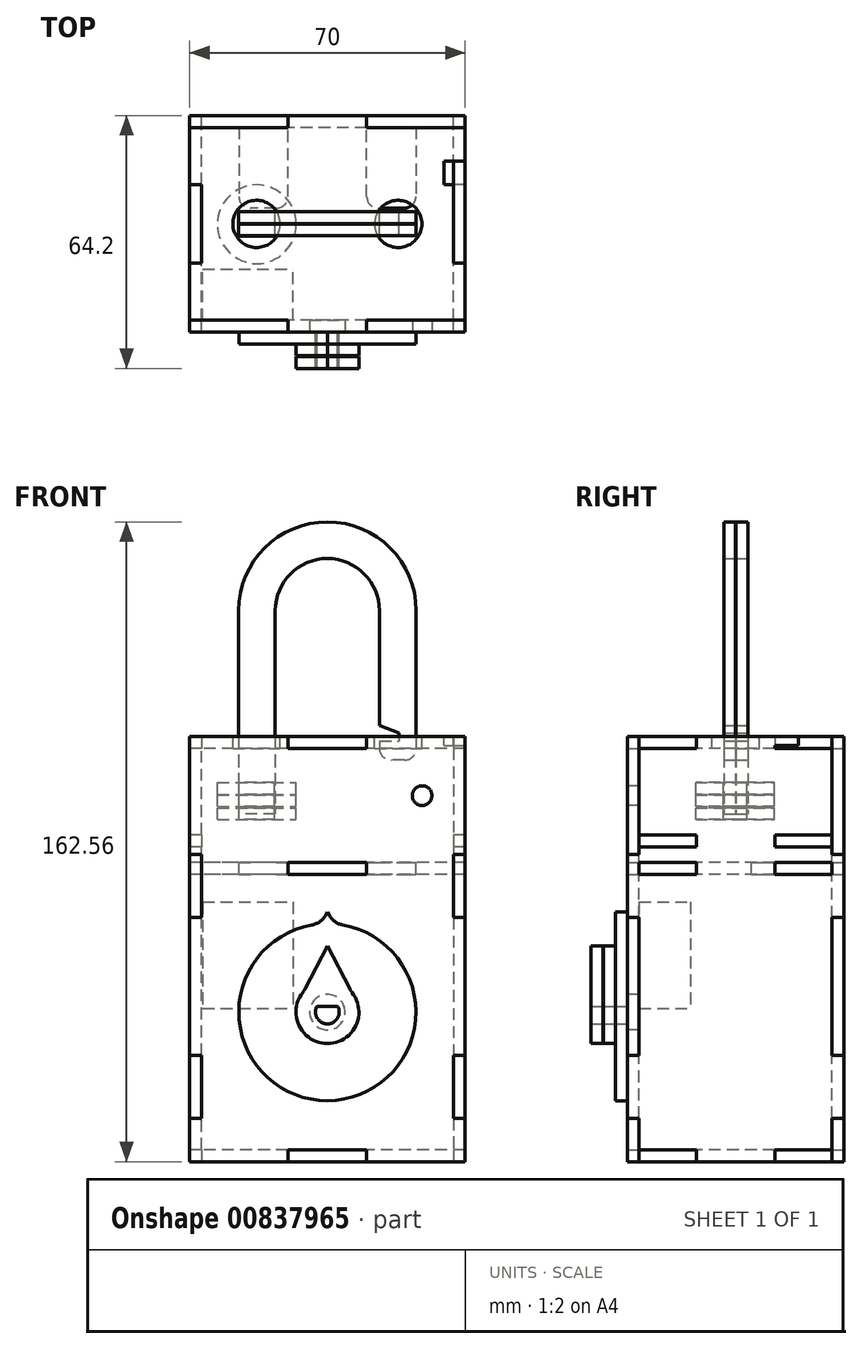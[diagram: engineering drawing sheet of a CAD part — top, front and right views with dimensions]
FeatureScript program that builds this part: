
annotation { "Feature Type Name" : "Feature", "Feature Type Description" : "" }
export const myFeature = defineFeature(function(context is Context, id is Id, definition is map)
    precondition{}
    {
        {
            assignVariable(context, id + "F0", {"name" : "w", "anyValue" : 3});
        }
        {
            var Q0;
            Q0=qCreatedBy(makeId("Front.planeOp"),FACE);
            var sketch = newSketch(context, id + "F1", { "sketchPlane" : qUnion([Q0])});
            skLineSegment(sketch, "E0.bottom", {"start": v(35, -38) * mm, "end": v(10, -38) * mm});
            skLineSegment(sketch, "E0.top", {"start": v(35, 70) * mm, "end": v(10, 70) * mm});
            skLineSegment(sketch, "E0.left", {"start": v(35, -38) * mm, "end": v(35, -27) * mm});
            skPoint(sketch, "E0.middle", {"position": v(0, 0) * mm});
            skLineSegment(sketch, "E1", {"start": v(35, -38) * mm, "end": v(35, -27) * mm, "construction": true});
            skLineSegment(sketch, "E2.bottom", {"start": v(32, -27) * mm, "end": v(35, -27) * mm});
            skLineSegment(sketch, "E2.top", {"start": v(32, -11) * mm, "end": v(35, -11) * mm});
            skLineSegment(sketch, "E2.left", {"start": v(32, -27) * mm, "end": v(32, -11) * mm});
            skLineSegment(sketch, "E3.bottom", {"start": v(35, 24) * mm, "end": v(32, 24) * mm});
            skLineSegment(sketch, "E3.top", {"start": v(35, 40) * mm, "end": v(32, 40) * mm});
            skLineSegment(sketch, "E3.right", {"start": v(32, 24) * mm, "end": v(32, 40) * mm});
            skLineSegment(sketch, "E4.trimOffspring", {"start": v(35, 40) * mm, "end": v(35, 51) * mm});
            skLineSegment(sketch, "E5.trimOffspring", {"start": v(35, -11) * mm, "end": v(35, 24) * mm});
            skLineSegment(sketch, "E6", {"start": v(0, 38) * mm, "end": v(0, -38) * mm, "construction": true});
            skLineSegment(sketch, "E7.bottom", {"start": v(10, 67) * mm, "end": v(-10, 67) * mm});
            skLineSegment(sketch, "E7.left", {"start": v(10, 67) * mm, "end": v(10, 70) * mm});
            skLineSegment(sketch, "E7.right", {"start": v(-10, 67) * mm, "end": v(-10, 70) * mm});
            skLineSegment(sketch, "E8.trimOffspring", {"start": v(-10, 70) * mm, "end": v(-35, 70) * mm});
            skLineSegment(sketch, "E9.bottom", {"start": v(10, -35) * mm, "end": v(-10, -35) * mm});
            skLineSegment(sketch, "E9.left", {"start": v(10, -35) * mm, "end": v(10, -38) * mm});
            skLineSegment(sketch, "E9.right", {"start": v(-10, -35) * mm, "end": v(-10, -38) * mm});
            skLineSegment(sketch, "E10.trimOffspring", {"start": v(-10, -38) * mm, "end": v(-35, -38) * mm});
            skLineSegment(sketch, "E11.MirrorCS", {"start": v(-32, -11) * mm, "end": v(-35, -11) * mm});
            skLineSegment(sketch, "E12.MirrorCS", {"start": v(-32, -27) * mm, "end": v(-35, -27) * mm});
            skLineSegment(sketch, "E13.MirrorCS", {"start": v(-35, 40) * mm, "end": v(-32, 40) * mm});
            skLineSegment(sketch, "E14.MirrorCS", {"start": v(-35, 24) * mm, "end": v(-32, 24) * mm});
            skLineSegment(sketch, "E15.MirrorCS", {"start": v(-35, -38) * mm, "end": v(-35, -27) * mm});
            skLineSegment(sketch, "E16.MirrorCS", {"start": v(-35, -38) * mm, "end": v(-35, -27) * mm, "construction": true});
            skLineSegment(sketch, "E17.MirrorCS", {"start": v(-35, 40) * mm, "end": v(-35, 51) * mm});
            skLineSegment(sketch, "E18.MirrorCS", {"start": v(-35, -11) * mm, "end": v(-35, 24) * mm});
            skLineSegment(sketch, "E19.MirrorCS", {"start": v(-32, 24) * mm, "end": v(-32, 40) * mm});
            skLineSegment(sketch, "E20.MirrorCS", {"start": v(-32, -27) * mm, "end": v(-32, -11) * mm});
            skLineSegment(sketch, "E21", {"start": v(-35, 40) * mm, "end": v(-35, 70) * mm});
            skLineSegment(sketch, "E22", {"start": v(35, 70) * mm, "end": v(35, 40) * mm});
            skSolve(sketch);
        }
        {
            var Q0;
            Q0=makeQuery(id+"F1.imprint","IMPRINT",FACE,{"disambiguationData":[TD([[makeQuery(id+"F1.imprint","IMPRINT",EDGE,{"derivedFrom":sQuery(id+"F1.wireOp",EDGE,"E0.bottom")}),-1.0]])]});
            extrude(context, id + "F2", {"entities" : qUnion([Q0]), "depth" : (getVariable(context, 'w')) * mm, "offsetDistance" : 25 * mm});
        }
        {
            var Q0;
            Q0=makeQuery(id+"F2.opExtrude","SWEPT_FACE",FACE,{"disambiguationData":[OSD([sQuery(id+"F1.wireOp",EDGE,"E0.left")])]});
            var sketch = newSketch(context, id + "F3", { "sketchPlane" : qUnion([Q0])});
            skLineSegment(sketch, "E23.bottom", {"start": v(0, -38) * mm, "end": v(-55, -38) * mm});
            skLineSegment(sketch, "E23.top", {"start": v(0, 70) * mm, "end": v(-55, 70) * mm});
            skLineSegment(sketch, "E23.left", {"start": v(0, -38) * mm, "end": v(0, 70) * mm});
            skLineSegment(sketch, "E23.right", {"start": v(-55, -38) * mm, "end": v(-55, 70) * mm});
            skSolve(sketch);
        }
        {
            var Q0;
            Q0=makeQuery(id+"F2.opExtrude","SWEPT_FACE",FACE,{"disambiguationData":[OSD([sQuery(id+"F1.wireOp",EDGE,"E0.bottom")])]});
            var sketch = newSketch(context, id + "F4", { "sketchPlane" : qUnion([Q0])});
            skLineSegment(sketch, "E24.left", {"start": v(35, 0) * mm, "end": v(35, 17.5) * mm});
            skLineSegment(sketch, "E25.MirrorCS", {"start": v(35, 55) * mm, "end": v(-35, 55) * mm});
            skLineSegment(sketch, "E26.MirrorCS", {"start": v(-35, 0) * mm, "end": v(-35, 17.5) * mm});
            skLineSegment(sketch, "E27.MirrorCS", {"start": v(35, 0) * mm, "end": v(-35, 0) * mm});
            skLineSegment(sketch, "E28", {"start": v(35, 55) * mm, "end": v(32, 55) * mm, "construction": true});
            skLineSegment(sketch, "E29", {"start": v(32, 55) * mm, "end": v(32, 0) * mm, "construction": true});
            skLineSegment(sketch, "E30", {"start": v(-35, 55) * mm, "end": v(-32, 55) * mm, "construction": true});
            skLineSegment(sketch, "E31", {"start": v(-32, 55) * mm, "end": v(-32, 0) * mm, "construction": true});
            skLineSegment(sketch, "E32", {"start": v(-35, 27.5) * mm, "end": v(35, 27.5) * mm, "construction": true});
            skLineSegment(sketch, "E33.bottom", {"start": v(35, 17.5) * mm, "end": v(32, 17.5) * mm});
            skLineSegment(sketch, "E33.top", {"start": v(35, 37.5) * mm, "end": v(32, 37.5) * mm});
            skLineSegment(sketch, "E33.right", {"start": v(32, 17.5) * mm, "end": v(32, 37.5) * mm});
            skLineSegment(sketch, "E34.bottom", {"start": v(-32, 17.5) * mm, "end": v(-35, 17.5) * mm});
            skLineSegment(sketch, "E34.top", {"start": v(-32, 37.5) * mm, "end": v(-35, 37.5) * mm});
            skLineSegment(sketch, "E34.left", {"start": v(-32, 17.5) * mm, "end": v(-32, 37.5) * mm});
            skLineSegment(sketch, "E35.trimOffspring", {"start": v(-35, 37.5) * mm, "end": v(-35, 55) * mm});
            skLineSegment(sketch, "E36.trimOffspring", {"start": v(35, 37.5) * mm, "end": v(35, 55) * mm});
            skSolve(sketch);
        }
        {
            var Q0;
            Q0 = qSketchRegion(id + "F3", true);
            extrude(context, id + "F5", {"entities" : qUnion([Q0]), "oppositeDirection" : true, "depth" : (getVariable(context, 'w')) * mm, "offsetDistance" : 25 * mm});
        }
        {
            var Q0;
            Q0 = qSketchRegion(id + "F4", true);
            extrude(context, id + "F6", {"entities" : qUnion([Q0]), "oppositeDirection" : true, "depth" : (getVariable(context, 'w')) * mm, "offsetDistance" : 25 * mm});
        }
        {
            var Q0;
            Q0=makeQuery(id+"F2.opExtrude","SWEPT_BODY",BODY,{"disambiguationData":[OSD([sQuery(id+"F1.wireOp",EDGE,"E0.bottom"),sQuery(id+"F1.wireOp",EDGE,"E0.top"),sQuery(id+"F1.wireOp",EDGE,"E0.left"),sQuery(id+"F1.wireOp",EDGE,"E2.bottom"),sQuery(id+"F1.wireOp",EDGE,"E2.top"),sQuery(id+"F1.wireOp",EDGE,"E2.left"),sQuery(id+"F1.wireOp",EDGE,"E3.bottom"),sQuery(id+"F1.wireOp",EDGE,"E3.top"),sQuery(id+"F1.wireOp",EDGE,"E3.right"),sQuery(id+"F1.wireOp",EDGE,"E4.trimOffspring"),sQuery(id+"F1.wireOp",EDGE,"E5.trimOffspring"),sQuery(id+"F1.wireOp",EDGE,"E7.bottom"),sQuery(id+"F1.wireOp",EDGE,"E7.left"),sQuery(id+"F1.wireOp",EDGE,"E7.right"),sQuery(id+"F1.wireOp",EDGE,"E8.trimOffspring"),sQuery(id+"F1.wireOp",EDGE,"E9.bottom"),sQuery(id+"F1.wireOp",EDGE,"E9.left"),sQuery(id+"F1.wireOp",EDGE,"E9.right"),sQuery(id+"F1.wireOp",EDGE,"E10.trimOffspring"),sQuery(id+"F1.wireOp",EDGE,"E11.MirrorCS"),sQuery(id+"F1.wireOp",EDGE,"E12.MirrorCS"),sQuery(id+"F1.wireOp",EDGE,"E13.MirrorCS"),sQuery(id+"F1.wireOp",EDGE,"E14.MirrorCS"),sQuery(id+"F1.wireOp",EDGE,"E15.MirrorCS"),sQuery(id+"F1.wireOp",EDGE,"E17.MirrorCS"),sQuery(id+"F1.wireOp",EDGE,"E18.MirrorCS"),sQuery(id+"F1.wireOp",EDGE,"E19.MirrorCS"),sQuery(id+"F1.wireOp",EDGE,"E20.MirrorCS")])]});
            transform(context, id + "F7", {"entities" : qUnion([Q0]), "transformType" : TransformType.TRANSLATION_3D, "dx" : 0 * mm, "dy" : -52 * mm, "dz" : 0 * mm, "makeCopy" : true});
        }
        {
            var Q0;
            Q0=makeQuery(id+"F2.opExtrude","SWEPT_BODY",BODY,{"disambiguationData":[OSD([sQuery(id+"F1.wireOp",EDGE,"E0.bottom"),sQuery(id+"F1.wireOp",EDGE,"E0.top"),sQuery(id+"F1.wireOp",EDGE,"E0.left"),sQuery(id+"F1.wireOp",EDGE,"E2.bottom"),sQuery(id+"F1.wireOp",EDGE,"E2.top"),sQuery(id+"F1.wireOp",EDGE,"E2.left"),sQuery(id+"F1.wireOp",EDGE,"E3.bottom"),sQuery(id+"F1.wireOp",EDGE,"E3.top"),sQuery(id+"F1.wireOp",EDGE,"E3.right"),sQuery(id+"F1.wireOp",EDGE,"E4.trimOffspring"),sQuery(id+"F1.wireOp",EDGE,"E5.trimOffspring"),sQuery(id+"F1.wireOp",EDGE,"E7.bottom"),sQuery(id+"F1.wireOp",EDGE,"E7.left"),sQuery(id+"F1.wireOp",EDGE,"E7.right"),sQuery(id+"F1.wireOp",EDGE,"E8.trimOffspring"),sQuery(id+"F1.wireOp",EDGE,"E9.bottom"),sQuery(id+"F1.wireOp",EDGE,"E9.left"),sQuery(id+"F1.wireOp",EDGE,"E9.right"),sQuery(id+"F1.wireOp",EDGE,"E10.trimOffspring"),sQuery(id+"F1.wireOp",EDGE,"E11.MirrorCS"),sQuery(id+"F1.wireOp",EDGE,"E12.MirrorCS"),sQuery(id+"F1.wireOp",EDGE,"E13.MirrorCS"),sQuery(id+"F1.wireOp",EDGE,"E14.MirrorCS"),sQuery(id+"F1.wireOp",EDGE,"E15.MirrorCS"),sQuery(id+"F1.wireOp",EDGE,"E17.MirrorCS"),sQuery(id+"F1.wireOp",EDGE,"E18.MirrorCS"),sQuery(id+"F1.wireOp",EDGE,"E19.MirrorCS"),sQuery(id+"F1.wireOp",EDGE,"E20.MirrorCS")])]});
            var Q1;
            Q1=makeQuery(id+"F7.opPattern","COPY",BODY,{"derivedFrom":makeQuery(id+"F2.opExtrude","SWEPT_BODY",BODY,{"disambiguationData":[OSD([sQuery(id+"F1.wireOp",EDGE,"E0.bottom"),sQuery(id+"F1.wireOp",EDGE,"E0.top"),sQuery(id+"F1.wireOp",EDGE,"E0.left"),sQuery(id+"F1.wireOp",EDGE,"E2.bottom"),sQuery(id+"F1.wireOp",EDGE,"E2.top"),sQuery(id+"F1.wireOp",EDGE,"E2.left"),sQuery(id+"F1.wireOp",EDGE,"E3.bottom"),sQuery(id+"F1.wireOp",EDGE,"E3.top"),sQuery(id+"F1.wireOp",EDGE,"E3.right"),sQuery(id+"F1.wireOp",EDGE,"E4.trimOffspring"),sQuery(id+"F1.wireOp",EDGE,"E5.trimOffspring"),sQuery(id+"F1.wireOp",EDGE,"E7.bottom"),sQuery(id+"F1.wireOp",EDGE,"E7.left"),sQuery(id+"F1.wireOp",EDGE,"E7.right"),sQuery(id+"F1.wireOp",EDGE,"E8.trimOffspring"),sQuery(id+"F1.wireOp",EDGE,"E9.bottom"),sQuery(id+"F1.wireOp",EDGE,"E9.left"),sQuery(id+"F1.wireOp",EDGE,"E9.right"),sQuery(id+"F1.wireOp",EDGE,"E10.trimOffspring"),sQuery(id+"F1.wireOp",EDGE,"E11.MirrorCS"),sQuery(id+"F1.wireOp",EDGE,"E12.MirrorCS"),sQuery(id+"F1.wireOp",EDGE,"E13.MirrorCS"),sQuery(id+"F1.wireOp",EDGE,"E14.MirrorCS"),sQuery(id+"F1.wireOp",EDGE,"E15.MirrorCS"),sQuery(id+"F1.wireOp",EDGE,"E17.MirrorCS"),sQuery(id+"F1.wireOp",EDGE,"E18.MirrorCS"),sQuery(id+"F1.wireOp",EDGE,"E19.MirrorCS"),sQuery(id+"F1.wireOp",EDGE,"E20.MirrorCS")])]}),"instanceName":"1"});
            var Q2;
            Q2=makeQuery(id+"F5.opExtrude","SWEPT_BODY",BODY,{"disambiguationData":[OSD([sQuery(id+"F3.wireOp",EDGE,"E23.bottom"),sQuery(id+"F3.wireOp",EDGE,"E23.top"),sQuery(id+"F3.wireOp",EDGE,"E23.left"),sQuery(id+"F3.wireOp",EDGE,"E23.right")])]});
            var Q3;
            Q3=makeQuery(id+"F6.opExtrude","SWEPT_BODY",BODY,{"disambiguationData":[OSD([sQuery(id+"F4.wireOp",EDGE,"E24.left"),sQuery(id+"F4.wireOp",EDGE,"E25.MirrorCS"),sQuery(id+"F4.wireOp",EDGE,"E26.MirrorCS"),sQuery(id+"F4.wireOp",EDGE,"E27.MirrorCS")])]});
            booleanBodies(context, id + "F8", {"operationType" : BooleanOperationType.SUBTRACTION, "tools" : qUnion([Q0, Q1]), "targets" : qUnion([Q2, Q3]), "keepTools" : true});
        }
        {
            var Q0;
            Q0=makeQuery(id+"F5.opExtrude","SWEPT_BODY",BODY,{"disambiguationData":[OSD([sQuery(id+"F3.wireOp",EDGE,"E23.bottom"),sQuery(id+"F3.wireOp",EDGE,"E23.top"),sQuery(id+"F3.wireOp",EDGE,"E23.left"),sQuery(id+"F3.wireOp",EDGE,"E23.right")])]});
            transform(context, id + "F9", {"entities" : qUnion([Q0]), "transformType" : TransformType.TRANSLATION_3D, "dx" : -67 * mm, "dy" : 0 * mm, "dz" : 0 * mm, "makeCopy" : true});
        }
        {
            var Q0;
            Q0=makeQuery(id+"F6.opExtrude","SWEPT_BODY",BODY,{"disambiguationData":[OSD([sQuery(id+"F4.wireOp",EDGE,"E24.left"),sQuery(id+"F4.wireOp",EDGE,"E25.MirrorCS"),sQuery(id+"F4.wireOp",EDGE,"E26.MirrorCS"),sQuery(id+"F4.wireOp",EDGE,"E27.MirrorCS"),sQuery(id+"F4.wireOp",EDGE,"E33.bottom"),sQuery(id+"F4.wireOp",EDGE,"E33.top"),sQuery(id+"F4.wireOp",EDGE,"E33.right"),sQuery(id+"F4.wireOp",EDGE,"E34.bottom"),sQuery(id+"F4.wireOp",EDGE,"E34.top"),sQuery(id+"F4.wireOp",EDGE,"E34.left"),sQuery(id+"F4.wireOp",EDGE,"E35.trimOffspring"),sQuery(id+"F4.wireOp",EDGE,"E36.trimOffspring")])]});
            var Q1;
            Q1=makeQuery(id+"F9.opPattern","COPY",BODY,{"derivedFrom":makeQuery(id+"F5.opExtrude","SWEPT_BODY",BODY,{"disambiguationData":[OSD([sQuery(id+"F3.wireOp",EDGE,"E23.bottom"),sQuery(id+"F3.wireOp",EDGE,"E23.top"),sQuery(id+"F3.wireOp",EDGE,"E23.left"),sQuery(id+"F3.wireOp",EDGE,"E23.right")])]}),"instanceName":"1"});
            var Q2;
            Q2=makeQuery(id+"F5.opExtrude","SWEPT_BODY",BODY,{"disambiguationData":[OSD([sQuery(id+"F3.wireOp",EDGE,"E23.bottom"),sQuery(id+"F3.wireOp",EDGE,"E23.top"),sQuery(id+"F3.wireOp",EDGE,"E23.left"),sQuery(id+"F3.wireOp",EDGE,"E23.right")])]});
            booleanBodies(context, id + "F10", {"operationType" : BooleanOperationType.SUBTRACTION, "tools" : qUnion([Q0]), "targets" : qUnion([Q1, Q2]), "keepTools" : true});
        }
        {
            var Q0;
            Q0=makeQuery(id+"F6.opExtrude","SWEPT_BODY",BODY,{"disambiguationData":[OSD([sQuery(id+"F4.wireOp",EDGE,"E24.left"),sQuery(id+"F4.wireOp",EDGE,"E25.MirrorCS"),sQuery(id+"F4.wireOp",EDGE,"E26.MirrorCS"),sQuery(id+"F4.wireOp",EDGE,"E27.MirrorCS"),sQuery(id+"F4.wireOp",EDGE,"E33.bottom"),sQuery(id+"F4.wireOp",EDGE,"E33.top"),sQuery(id+"F4.wireOp",EDGE,"E33.right"),sQuery(id+"F4.wireOp",EDGE,"E34.bottom"),sQuery(id+"F4.wireOp",EDGE,"E34.top"),sQuery(id+"F4.wireOp",EDGE,"E34.left"),sQuery(id+"F4.wireOp",EDGE,"E35.trimOffspring"),sQuery(id+"F4.wireOp",EDGE,"E36.trimOffspring")])]});
            transform(context, id + "F11", {"entities" : qUnion([Q0]), "transformType" : TransformType.TRANSLATION_3D, "dx" : 0 * mm, "dy" : 0 * mm, "dz" : 80 * mm, "makeCopy" : true});
        }
        {
            var Q0;
            Q0=makeQuery(id+"F11.opPattern","COPY",BODY,{"derivedFrom":makeQuery(id+"F6.opExtrude","SWEPT_BODY",BODY,{"disambiguationData":[OSD([sQuery(id+"F4.wireOp",EDGE,"E24.left"),sQuery(id+"F4.wireOp",EDGE,"E25.MirrorCS"),sQuery(id+"F4.wireOp",EDGE,"E26.MirrorCS"),sQuery(id+"F4.wireOp",EDGE,"E27.MirrorCS"),sQuery(id+"F4.wireOp",EDGE,"E33.bottom"),sQuery(id+"F4.wireOp",EDGE,"E33.top"),sQuery(id+"F4.wireOp",EDGE,"E33.right"),sQuery(id+"F4.wireOp",EDGE,"E34.bottom"),sQuery(id+"F4.wireOp",EDGE,"E34.top"),sQuery(id+"F4.wireOp",EDGE,"E34.left"),sQuery(id+"F4.wireOp",EDGE,"E35.trimOffspring"),sQuery(id+"F4.wireOp",EDGE,"E36.trimOffspring")])]}),"instanceName":"1"});
            var Q1;
            Q1=makeQuery(id+"F9.opPattern","COPY",BODY,{"derivedFrom":makeQuery(id+"F5.opExtrude","SWEPT_BODY",BODY,{"disambiguationData":[OSD([sQuery(id+"F3.wireOp",EDGE,"E23.bottom"),sQuery(id+"F3.wireOp",EDGE,"E23.top"),sQuery(id+"F3.wireOp",EDGE,"E23.left"),sQuery(id+"F3.wireOp",EDGE,"E23.right")])]}),"instanceName":"1"});
            var Q2;
            Q2=makeQuery(id+"F5.opExtrude","SWEPT_BODY",BODY,{"disambiguationData":[OSD([sQuery(id+"F3.wireOp",EDGE,"E23.bottom"),sQuery(id+"F3.wireOp",EDGE,"E23.top"),sQuery(id+"F3.wireOp",EDGE,"E23.left"),sQuery(id+"F3.wireOp",EDGE,"E23.right")])]});
            booleanBodies(context, id + "F12", {"operationType" : BooleanOperationType.SUBTRACTION, "tools" : qUnion([Q0]), "targets" : qUnion([Q1, Q2]), "keepTools" : true});
        }
        {
            var Q0;
            Q0=makeQuery(id+"F11.opPattern","COPY",FACE,{"derivedFrom":makeQuery(id+"F6.opExtrude","CAP_FACE",FACE,{"disambiguationData":[OSD([sQuery(id+"F4.wireOp",EDGE,"E24.left"),sQuery(id+"F4.wireOp",EDGE,"E25.MirrorCS"),sQuery(id+"F4.wireOp",EDGE,"E26.MirrorCS"),sQuery(id+"F4.wireOp",EDGE,"E27.MirrorCS"),sQuery(id+"F4.wireOp",EDGE,"E33.bottom"),sQuery(id+"F4.wireOp",EDGE,"E33.top"),sQuery(id+"F4.wireOp",EDGE,"E33.right"),sQuery(id+"F4.wireOp",EDGE,"E34.bottom"),sQuery(id+"F4.wireOp",EDGE,"E34.top"),sQuery(id+"F4.wireOp",EDGE,"E34.left"),sQuery(id+"F4.wireOp",EDGE,"E35.trimOffspring"),sQuery(id+"F4.wireOp",EDGE,"E36.trimOffspring")])],"isStart":false}),"instanceName":"1"});
            var sketch = newSketch(context, id + "F13", { "sketchPlane" : qUnion([Q0])});
            skLineSegment(sketch, "E37", {"start": v(0, -27.5) * mm, "end": v(18, -27.5) * mm, "construction": true});
            skLineSegment(sketch, "E38", {"start": v(18, -27.5) * mm, "end": v(-18, -27.5) * mm, "construction": true});
            skCircle(sketch, "E39", {"center": v(-18, -27.5) * mm, "radius": 6 * mm});
            skCircle(sketch, "E40", {"center": v(18, -27.5) * mm, "radius": 6 * mm});
            skSolve(sketch);
        }
        {
            var Q0;
            Q0=makeQuery(id+"F13.imprint","IMPRINT",FACE,{"disambiguationData":[TD([[makeQuery(id+"F13.imprint","IMPRINT",EDGE,{"derivedFrom":sQuery(id+"F13.wireOp",EDGE,"E39")}),1.0]])]});
            var Q1;
            Q1=makeQuery(id+"F13.imprint","IMPRINT",FACE,{"disambiguationData":[TD([[makeQuery(id+"F13.imprint","IMPRINT",EDGE,{"derivedFrom":sQuery(id+"F13.wireOp",EDGE,"E40")}),1.0]])]});
            var Q2;
            Q2=sQuery(id+"F13.wireOp",EDGE,"E39");
            var Q3;
            Q3=sQuery(id+"F13.wireOp",EDGE,"E40");
            extrude(context, id + "F14", {"entities" : qUnion([Q0, Q1]), "operationType" : NewBodyOperationType.REMOVE, "surfaceEntities" : qUnion([Q2, Q3]), "oppositeDirection" : true, "depth" : 25 * mm, "offsetDistance" : 25 * mm});
        }
        {
            var Q0;
            Q0=makeQuery(id+"F7.opPattern","COPY",FACE,{"derivedFrom":makeQuery(id+"F2.opExtrude","CAP_FACE",FACE,{"disambiguationData":[OSD([sQuery(id+"F1.wireOp",EDGE,"E0.bottom"),sQuery(id+"F1.wireOp",EDGE,"E0.top"),sQuery(id+"F1.wireOp",EDGE,"E0.left"),sQuery(id+"F1.wireOp",EDGE,"E2.bottom"),sQuery(id+"F1.wireOp",EDGE,"E2.top"),sQuery(id+"F1.wireOp",EDGE,"E2.left"),sQuery(id+"F1.wireOp",EDGE,"E3.bottom"),sQuery(id+"F1.wireOp",EDGE,"E3.top"),sQuery(id+"F1.wireOp",EDGE,"E3.right"),sQuery(id+"F1.wireOp",EDGE,"E4.trimOffspring"),sQuery(id+"F1.wireOp",EDGE,"E5.trimOffspring"),sQuery(id+"F1.wireOp",EDGE,"E7.bottom"),sQuery(id+"F1.wireOp",EDGE,"E7.left"),sQuery(id+"F1.wireOp",EDGE,"E7.right"),sQuery(id+"F1.wireOp",EDGE,"E8.trimOffspring"),sQuery(id+"F1.wireOp",EDGE,"E9.bottom"),sQuery(id+"F1.wireOp",EDGE,"E9.left"),sQuery(id+"F1.wireOp",EDGE,"E9.right"),sQuery(id+"F1.wireOp",EDGE,"E10.trimOffspring"),sQuery(id+"F1.wireOp",EDGE,"E11.MirrorCS"),sQuery(id+"F1.wireOp",EDGE,"E12.MirrorCS"),sQuery(id+"F1.wireOp",EDGE,"E13.MirrorCS"),sQuery(id+"F1.wireOp",EDGE,"E14.MirrorCS"),sQuery(id+"F1.wireOp",EDGE,"E15.MirrorCS"),sQuery(id+"F1.wireOp",EDGE,"E17.MirrorCS"),sQuery(id+"F1.wireOp",EDGE,"E18.MirrorCS"),sQuery(id+"F1.wireOp",EDGE,"E19.MirrorCS"),sQuery(id+"F1.wireOp",EDGE,"E20.MirrorCS")])],"isStart":false}),"instanceName":"1"});
            var sketch = newSketch(context, id + "F15", { "sketchPlane" : qUnion([Q0])});
            skArc(sketch, "E41", {"start": v(-6.24, 5) * mm, "mid": v(0, -8) * mm, "end": v(6.24, 5) * mm});
            skArc(sketch, "E42", {"start": v(-3.93, 22.15) * mm, "mid": v(0.02, -22.5) * mm, "end": v(3.9, 22.16) * mm});
            skLineSegment(sketch, "E43", {"start": v(0, 0) * mm, "end": v(0, 25.4) * mm, "construction": true});
            skLineSegment(sketch, "E44", {"start": v(0, 25.4) * mm, "end": v(-0.46, 24.6) * mm});
            skLineSegment(sketch, "E45", {"start": v(0, 25.4) * mm, "end": v(0.5, 24.53) * mm});
            skPoint(sketch, "E46.visualSharp", {"position": v(-1.7, 22.44) * mm});
            skArc(sketch, "E46.filletArc", {"start": v(-3.93, 22.15) * mm, "mid": v(-1.92, 23) * mm, "end": v(-0.46, 24.6) * mm});
            skPoint(sketch, "E47.visualSharp", {"position": v(1.72, 22.43) * mm});
            skArc(sketch, "E47.filletArc", {"start": v(0.5, 24.53) * mm, "mid": v(1.94, 22.97) * mm, "end": v(3.9, 22.16) * mm});
            skCircle(sketch, "E48", {"center": v(0, 0) * mm, "radius": 4.5 * mm});
            skArc(sketch, "E49", {"start": v(-2.6, 1.5) * mm, "mid": v(0, -3) * mm, "end": v(2.6, 1.5) * mm});
            skLineSegment(sketch, "E50", {"start": v(0, 0) * mm, "end": v(0, 1.5) * mm, "construction": true});
            skLineSegment(sketch, "E51", {"start": v(0, 1.5) * mm, "end": v(2.6, 1.5) * mm, "construction": true});
            skLineSegment(sketch, "E52", {"start": v(2.6, 1.5) * mm, "end": v(-2.6, 1.5) * mm});
            skLineSegment(sketch, "E53", {"start": v(0, 16.88) * mm, "end": v(-5.7, 5.83) * mm});
            skLineSegment(sketch, "E54", {"start": v(5.7, 5.83) * mm, "end": v(0, 16.88) * mm});
            skPoint(sketch, "E55.visualSharp", {"position": v(-5.96, 5.34) * mm});
            skArc(sketch, "E55.filletArc", {"start": v(-6.24, 5) * mm, "mid": v(-5.95, 5.4) * mm, "end": v(-5.7, 5.83) * mm});
            skPoint(sketch, "E56.visualSharp", {"position": v(5.96, 5.34) * mm});
            skArc(sketch, "E56.filletArc", {"start": v(5.7, 5.83) * mm, "mid": v(5.95, 5.4) * mm, "end": v(6.24, 5) * mm});
            skSolve(sketch);
        }
        {
            var Q0;
            Q0=makeQuery(id+"F15.imprint","IMPRINT",FACE,{"disambiguationData":[TD([[makeQuery(id+"F15.imprint","IMPRINT",EDGE,{"derivedFrom":sQuery(id+"F15.wireOp",EDGE,"E48")}),1.0]])]});
            var Q1;
            Q1=makeQuery(id+"F15.imprint","IMPRINT",FACE,{"disambiguationData":[TD([[makeQuery(id+"F15.imprint","IMPRINT",EDGE,{"derivedFrom":sQuery(id+"F15.wireOp",EDGE,"E49")}),1.0]])]});
            var Q2;
            Q2=sQuery(id+"F15.wireOp",EDGE,"E41");
            extrude(context, id + "F16", {"entities" : qUnion([Q0, Q1]), "operationType" : NewBodyOperationType.REMOVE, "surfaceEntities" : qUnion([Q2]), "oppositeDirection" : true, "depth" : 5 * mm, "offsetDistance" : 25 * mm});
        }
        {
            var Q0;
            Q0=makeQuery(id+"F15.imprint","IMPRINT",FACE,{"disambiguationData":[TD([[makeQuery(id+"F15.imprint","IMPRINT",EDGE,{"derivedFrom":sQuery(id+"F15.wireOp",EDGE,"E41")}),-1.0]])]});
            var Q1;
            Q1=makeQuery(id+"F15.imprint","IMPRINT",FACE,{"disambiguationData":[TD([[makeQuery(id+"F15.imprint","IMPRINT",EDGE,{"derivedFrom":sQuery(id+"F15.wireOp",EDGE,"E41")}),1.0]])]});
            var Q2;
            Q2=makeQuery(id+"F15.imprint","IMPRINT",FACE,{"disambiguationData":[TD([[makeQuery(id+"F15.imprint","IMPRINT",EDGE,{"derivedFrom":sQuery(id+"F15.wireOp",EDGE,"E48")}),1.0]])]});
            extrude(context, id + "F17", {"entities" : qUnion([Q0, Q1, Q2]), "depth" : (getVariable(context, 'w')) * mm, "offsetDistance" : 25 * mm});
        }
        {
            var Q0;
            Q0=makeQuery(id+"F15.imprint","IMPRINT",FACE,{"disambiguationData":[TD([[makeQuery(id+"F15.imprint","IMPRINT",EDGE,{"derivedFrom":sQuery(id+"F15.wireOp",EDGE,"E41")}),1.0]])]});
            var Q1;
            Q1=makeQuery(id+"F15.imprint","IMPRINT",FACE,{"disambiguationData":[TD([[makeQuery(id+"F15.imprint","IMPRINT",EDGE,{"derivedFrom":sQuery(id+"F15.wireOp",EDGE,"E48")}),1.0]])]});
            var Q2;
            Q2=sQuery(id+"F15.wireOp",EDGE,"E41");
            var Q3;
            Q3=sQuery(id+"F15.wireOp",EDGE,"E48");
            extrude(context, id + "F18", {"entities" : qUnion([Q0, Q1]), "surfaceEntities" : qUnion([Q2, Q3]), "depth" : 6 * mm, "offsetDistance" : 25 * mm, "hasSecondDirection" : true, "secondDirectionOppositeDirection" : false, "secondDirectionDepth" : 3 * mm});
        }
        {
            var Q0;
            Q0=makeQuery(id+"F15.imprint","IMPRINT",FACE,{"disambiguationData":[TD([[makeQuery(id+"F15.imprint","IMPRINT",EDGE,{"derivedFrom":sQuery(id+"F15.wireOp",EDGE,"E42")}),-1.0]])]});
            var sketch = newSketch(context, id + "F19", { "sketchPlane" : qUnion([Q0])});
            skArc(sketch, "E57", {"start": v(13.24, 102) * mm, "mid": v(0, 115.24) * mm, "end": v(-13.24, 102) * mm});
            skLineSegment(sketch, "E58", {"start": v(-13.24, 102) * mm, "end": v(-13.24, 54.66) * mm});
            skLineSegment(sketch, "E59", {"start": v(13.24, 102) * mm, "end": v(13.24, 72.88) * mm});
            skLineSegment(sketch, "E60", {"start": v(22.56, 102) * mm, "end": v(22.56, 67) * mm});
            skLineSegment(sketch, "E61", {"start": v(-22.56, 102) * mm, "end": v(-22.56, 50.39) * mm});
            skArc(sketch, "E62.trimOffspring", {"start": v(22.56, 102) * mm, "mid": v(0, 124.56) * mm, "end": v(-22.56, 102) * mm});
            skLineSegment(sketch, "E63", {"start": v(-13.24, 54.66) * mm, "end": v(-13.24, 50.39) * mm});
            skLineSegment(sketch, "E64", {"start": v(19.56, 64) * mm, "end": v(16.24, 64) * mm});
            skPoint(sketch, "E65.visualSharp", {"position": v(22.56, 64) * mm});
            skArc(sketch, "E65.filletArc", {"start": v(19.56, 64) * mm, "mid": v(21.68, 64.88) * mm, "end": v(22.56, 67) * mm});
            skPoint(sketch, "E66.visualSharp", {"position": v(13.24, 64) * mm});
            skArc(sketch, "E66.filletArc", {"start": v(13.24, 67) * mm, "mid": v(14.12, 64.88) * mm, "end": v(16.24, 64) * mm});
            skLineSegment(sketch, "E67.top", {"start": v(13.24, 68.88) * mm, "end": v(18.24, 68.88) * mm});
            skLineSegment(sketch, "E67.right", {"start": v(18.24, 70.88) * mm, "end": v(18.24, 68.88) * mm});
            skLineSegment(sketch, "E68", {"start": v(18.24, 70.88) * mm, "end": v(13.24, 72.88) * mm});
            skPoint(sketch, "E69.orphan", {"position": v(18.24, 72.88) * mm});
            skLineSegment(sketch, "E70.trimOffspring", {"start": v(13.24, 68.88) * mm, "end": v(13.24, 67) * mm});
            skLineSegment(sketch, "E71", {"start": v(-13.24, 50.39) * mm, "end": v(-22.56, 50.39) * mm});
            skSolve(sketch);
        }
        {
            var Q0;
            {var subQ8=sQuery(id+"F19.wireOp",EDGE,"E57");Q0=makeQuery(id+"F19.imprint","IMPRINT",FACE,{"disambiguationData":[TD([[makeQuery(id+"F19.imprint","IMPRINT",EDGE,{"derivedFrom":subQ8}),-1.0]])]});}
            var Q1;
            Q1=makeQuery(id+"F19.imprint","IMPRINT",FACE,{"disambiguationData":[TD([[makeQuery(id+"F19.imprint","IMPRINT",EDGE,{"derivedFrom":sQuery(id+"F19.wireOp",EDGE,"E64")}),-1.0]])]});
            var Q2;
            {var subQ4=sQuery(id+"F19.wireOp",EDGE,"E63");Q2=makeQuery(id+"F19.imprint","IMPRINT",FACE,{"disambiguationData":[TD([[makeQuery(id+"F19.imprint","IMPRINT",EDGE,{"derivedFrom":subQ4}),-1.0]])]});}
            extrude(context, id + "F20", {"entities" : qUnion([Q0, Q1, Q2]), "depth" : (getVariable(context, 'w')) * mm, "offsetDistance" : 25 * mm});
        }
        {
            var Q0;
            Q0=makeQuery(id+"F20.opExtrude","SWEPT_BODY",BODY,{"disambiguationData":[OSD([sQuery(id+"F19.wireOp",EDGE,"E57"),sQuery(id+"F19.wireOp",EDGE,"E58"),sQuery(id+"F19.wireOp",EDGE,"E59"),sQuery(id+"F19.wireOp",EDGE,"E60"),sQuery(id+"F19.wireOp",EDGE,"E61"),sQuery(id+"F19.wireOp",EDGE,"E62.trimOffspring"),sQuery(id+"F19.wireOp",EDGE,"cZzg15dB-Nbx1-w7XY-uspp-L3SwX9o6WefN"),sQuery(id+"F19.wireOp",EDGE,"treZg7xo-gXZQ-1tuO-3OQy-4RqyVRKiaork"),sQuery(id+"F19.wireOp",EDGE,"E63"),sQuery(id+"F19.wireOp",EDGE,"R1Tcik5A-y3kw-4I4Y-LH2I-3jnCuK7BDUFd"),sQuery(id+"F19.wireOp",EDGE,"49c95767-d3e9-4f83-846b-7651090b67ab.trimOffspring")])]});
            deleteBodies(context, id + "F21", {"entities" : qUnion([Q0])});
        }
        {
            var Q0;
            Q0=makeQuery(id+"F4.imprint","IMPRINT",FACE,{"disambiguationData":[TD([[makeQuery(id+"F4.imprint","IMPRINT",EDGE,{"derivedFrom":sQuery(id+"F4.wireOp",EDGE,"E25.MirrorCS")}),1.0]])]});
            var sketch = newSketch(context, id + "F22", { "sketchPlane" : qUnion([Q0])});
            skCircle(sketch, "E72", {"center": v(-17.94, 27.59) * mm, "radius": 10 * mm});
            skLineSegment(sketch, "E73.bottom", {"start": v(-13.44, 24.59) * mm, "end": v(-22.44, 24.59) * mm});
            skLineSegment(sketch, "E73.top", {"start": v(-13.44, 30.59) * mm, "end": v(-22.44, 30.59) * mm});
            skLineSegment(sketch, "E73.left", {"start": v(-13.44, 24.59) * mm, "end": v(-13.44, 30.59) * mm});
            skLineSegment(sketch, "E73.right", {"start": v(-22.44, 24.59) * mm, "end": v(-22.44, 30.59) * mm});
            skSolve(sketch);
        }
        {
            var Q0;
            Q0=makeQuery(id+"F22.imprint","IMPRINT",FACE,{"disambiguationData":[TD([[makeQuery(id+"F22.imprint","IMPRINT",EDGE,{"derivedFrom":sQuery(id+"F22.wireOp",EDGE,"E72")}),1.0]])]});
            extrude(context, id + "F23", {"entities" : qUnion([Q0]), "depth" : (getVariable(context, 'w')) * mm, "offsetDistance" : 25 * mm});
        }
        {
            var Q0;
            Q0=makeQuery(id+"F23.opExtrude","SWEPT_BODY",BODY,{"disambiguationData":[OSD([sQuery(id+"F22.wireOp",EDGE,"E72"),sQuery(id+"F22.wireOp",EDGE,"E73.bottom"),sQuery(id+"F22.wireOp",EDGE,"E73.top"),sQuery(id+"F22.wireOp",EDGE,"E73.left"),sQuery(id+"F22.wireOp",EDGE,"E73.right")])]});
            transform(context, id + "F24", {"entities" : qUnion([Q0]), "transformType" : TransformType.TRANSLATION_3D, "dx" : 0 * mm, "dy" : 0 * mm, "dz" : 68.2 * mm, "makeCopy" : true});
        }
        {
            var Q0;
            Q0=makeQuery(id+"F24.opPattern","COPY",BODY,{"derivedFrom":makeQuery(id+"F23.opExtrude","SWEPT_BODY",BODY,{"disambiguationData":[OSD([sQuery(id+"F22.wireOp",EDGE,"E72"),sQuery(id+"F22.wireOp",EDGE,"E73.bottom"),sQuery(id+"F22.wireOp",EDGE,"E73.top"),sQuery(id+"F22.wireOp",EDGE,"E73.left"),sQuery(id+"F22.wireOp",EDGE,"E73.right")])]}),"instanceName":"1"});
            transform(context, id + "F25", {"entities" : qUnion([Q0]), "transformType" : TransformType.TRANSLATION_3D, "dx" : 0 * mm, "dy" : 0 * mm, "dz" : -3.3 * mm, "makeCopy" : true});
        }
        {
            var Q0;
            Q0=makeQuery(id+"F25.opPattern","COPY",BODY,{"derivedFrom":makeQuery(id+"F24.opPattern","COPY",BODY,{"derivedFrom":makeQuery(id+"F23.opExtrude","SWEPT_BODY",BODY,{"disambiguationData":[OSD([sQuery(id+"F22.wireOp",EDGE,"E72"),sQuery(id+"F22.wireOp",EDGE,"E73.bottom"),sQuery(id+"F22.wireOp",EDGE,"E73.top"),sQuery(id+"F22.wireOp",EDGE,"E73.left"),sQuery(id+"F22.wireOp",EDGE,"E73.right")])]}),"instanceName":"1"}),"instanceName":"1"});
            transform(context, id + "F26", {"entities" : qUnion([Q0]), "transformType" : TransformType.TRANSLATION_3D, "dx" : 0 * mm, "dy" : 0 * mm, "dz" : 6.4 * mm, "makeCopy" : true});
        }
        {
            var Q0;
            Q0=makeQuery(id+"F23.opExtrude","SWEPT_BODY",BODY,{"disambiguationData":[OSD([sQuery(id+"F22.wireOp",EDGE,"E72"),sQuery(id+"F22.wireOp",EDGE,"E73.bottom"),sQuery(id+"F22.wireOp",EDGE,"E73.top"),sQuery(id+"F22.wireOp",EDGE,"E73.left"),sQuery(id+"F22.wireOp",EDGE,"E73.right")])]});
            deleteBodies(context, id + "F27", {"entities" : qUnion([Q0])});
        }
        {
            var Q0;
            Q0=makeQuery(id+"F5.opExtrude","CAP_FACE",FACE,{"disambiguationData":[OSD([sQuery(id+"F3.wireOp",EDGE,"E23.bottom"),sQuery(id+"F3.wireOp",EDGE,"E23.top"),sQuery(id+"F3.wireOp",EDGE,"E23.left"),sQuery(id+"F3.wireOp",EDGE,"E23.right")])],"isStart":true});
            var sketch = newSketch(context, id + "F28", { "sketchPlane" : qUnion([Q0])});
            skLineSegment(sketch, "E74.bottom", {"start": v(-11.5, 42.7) * mm, "end": v(-22.5, 42.7) * mm});
            skLineSegment(sketch, "E74.top", {"start": v(-11.5, 53.7) * mm, "end": v(-22.5, 53.7) * mm});
            skLineSegment(sketch, "E74.left", {"start": v(-11.5, 42.7) * mm, "end": v(-11.5, 53.7) * mm});
            skLineSegment(sketch, "E74.right", {"start": v(-22.5, 42.7) * mm, "end": v(-22.5, 53.7) * mm});
            skPoint(sketch, "E74.middle", {"position": v(-17, 48.2) * mm});
            skPoint(sketch, "E74.middle.positionSnap0", {"position": v(-27.5, 70) * mm});
            skPoint(sketch, "E74.centerSnap0", {"position": v(-27.5, 70) * mm});
            skSolve(sketch);
        }
        {
            var Q0;
            Q0=makeQuery(id+"F28.imprint","IMPRINT",FACE,{"disambiguationData":[TD([[makeQuery(id+"F28.imprint","IMPRINT",EDGE,{"derivedFrom":sQuery(id+"F28.wireOp",EDGE,"E74.bottom")}),-1.0]])]});
            extrude(context, id + "F29", {"entities" : qUnion([Q0]), "operationType" : NewBodyOperationType.REMOVE, "oppositeDirection" : true, "depth" : 5.4 * mm, "offsetDistance" : 25 * mm});
        }
        {
            var Q0;
            Q0=makeQuery(id+"F18.opExtrude","SWEPT_BODY",BODY,{"disambiguationData":[OSD([sQuery(id+"F15.wireOp",EDGE,"E41"),sQuery(id+"F15.wireOp",EDGE,"E49"),sQuery(id+"F15.wireOp",EDGE,"E52"),sQuery(id+"F15.wireOp",EDGE,"E53"),sQuery(id+"F15.wireOp",EDGE,"E54"),sQuery(id+"F15.wireOp",EDGE,"E55.filletArc"),sQuery(id+"F15.wireOp",EDGE,"E56.filletArc")])]});
            transform(context, id + "F30", {"entities" : qUnion([Q0]), "transformType" : TransformType.TRANSLATION_3D, "dx" : 0 * mm, "dy" : -3.2 * mm, "dz" : 0 * mm, "makeCopy" : true});
        }
        {
            var Q0;
            Q0=makeQuery(id+"F5.opExtrude","CAP_FACE",FACE,{"disambiguationData":[OSD([sQuery(id+"F3.wireOp",EDGE,"E23.bottom"),sQuery(id+"F3.wireOp",EDGE,"E23.top"),sQuery(id+"F3.wireOp",EDGE,"E23.left"),sQuery(id+"F3.wireOp",EDGE,"E23.right")])],"isStart":false});
            var sketch = newSketch(context, id + "F31", { "sketchPlane" : qUnion([Q0])});
            skLineSegment(sketch, "E75.bottom", {"start": v(52, 27.96) * mm, "end": v(39, 27.96) * mm});
            skLineSegment(sketch, "E75.top", {"start": v(52, 0.96) * mm, "end": v(39, 0.96) * mm});
            skLineSegment(sketch, "E75.left", {"start": v(52, 27.96) * mm, "end": v(52, 0.96) * mm});
            skLineSegment(sketch, "E75.right", {"start": v(39, 27.96) * mm, "end": v(39, 0.96) * mm});
            skSolve(sketch);
        }
        {
            var Q0;
            {var subQ9=sQuery(id+"F31.wireOp",EDGE,"E75.bottom");Q0=makeQuery(id+"F31.imprint","IMPRINT",FACE,{"disambiguationData":[TD([[makeQuery(id+"F31.imprint","IMPRINT",EDGE,{"derivedFrom":subQ9}),1.0]])]});}
            extrude(context, id + "F32", {"entities" : qUnion([Q0]), "depth" : 63.7 * mm, "offsetDistance" : 25 * mm, "hasSecondDirection" : true, "secondDirectionOppositeDirection" : false, "secondDirectionDepth" : (63.7 - 23) * mm});
        }
        {
            var Q0;
            Q0=makeQuery(id+"F15.imprint","IMPRINT",FACE,{"disambiguationData":[TD([[makeQuery(id+"F15.imprint","IMPRINT",EDGE,{"derivedFrom":sQuery(id+"F15.wireOp",EDGE,"E42")}),-1.0]])]});
            var sketch = newSketch(context, id + "F33", { "sketchPlane" : qUnion([Q0])});
            skCircle(sketch, "E76", {"center": v(24.06, 55) * mm, "radius": 2.5 * mm});
            skSolve(sketch);
        }
        {
            var Q0;
            Q0=makeQuery(id+"F33.imprint","IMPRINT",FACE,{"disambiguationData":[TD([[makeQuery(id+"F33.imprint","IMPRINT",EDGE,{"derivedFrom":sQuery(id+"F33.wireOp",EDGE,"E76")}),1.0]])]});
            var Q1;
            Q1=sQuery(id+"F33.wireOp",EDGE,"E76");
            extrude(context, id + "F34", {"entities" : qUnion([Q0]), "operationType" : NewBodyOperationType.REMOVE, "surfaceEntities" : qUnion([Q1]), "oppositeDirection" : true, "depth" : 6.1 * mm, "offsetDistance" : 25 * mm});
        }
        {
            var Q0;
            Q0=makeQuery(id+"F11.opPattern","COPY",BODY,{"derivedFrom":makeQuery(id+"F6.opExtrude","SWEPT_BODY",BODY,{"disambiguationData":[OSD([sQuery(id+"F4.wireOp",EDGE,"E24.left"),sQuery(id+"F4.wireOp",EDGE,"E25.MirrorCS"),sQuery(id+"F4.wireOp",EDGE,"E26.MirrorCS"),sQuery(id+"F4.wireOp",EDGE,"E27.MirrorCS"),sQuery(id+"F4.wireOp",EDGE,"E33.bottom"),sQuery(id+"F4.wireOp",EDGE,"E33.top"),sQuery(id+"F4.wireOp",EDGE,"E33.right"),sQuery(id+"F4.wireOp",EDGE,"E34.bottom"),sQuery(id+"F4.wireOp",EDGE,"E34.top"),sQuery(id+"F4.wireOp",EDGE,"E34.left"),sQuery(id+"F4.wireOp",EDGE,"E35.trimOffspring"),sQuery(id+"F4.wireOp",EDGE,"E36.trimOffspring")])]}),"instanceName":"1"});
            var Q1;
            Q1=makeQuery(id+"F11.opPattern","COPY",FACE,{"derivedFrom":makeQuery(id+"F6.opExtrude","CAP_FACE",FACE,{"disambiguationData":[OSD([sQuery(id+"F4.wireOp",EDGE,"E24.left"),sQuery(id+"F4.wireOp",EDGE,"E25.MirrorCS"),sQuery(id+"F4.wireOp",EDGE,"E26.MirrorCS"),sQuery(id+"F4.wireOp",EDGE,"E27.MirrorCS"),sQuery(id+"F4.wireOp",EDGE,"E33.bottom"),sQuery(id+"F4.wireOp",EDGE,"E33.top"),sQuery(id+"F4.wireOp",EDGE,"E33.right"),sQuery(id+"F4.wireOp",EDGE,"E34.bottom"),sQuery(id+"F4.wireOp",EDGE,"E34.top"),sQuery(id+"F4.wireOp",EDGE,"E34.left"),sQuery(id+"F4.wireOp",EDGE,"E35.trimOffspring"),sQuery(id+"F4.wireOp",EDGE,"E36.trimOffspring")])],"isStart":false}),"instanceName":"1"});
            transform(context, id + "F35", {"entities" : qUnion([Q0]), "transformType" : TransformType.TRANSLATION_DISTANCE, "transformDirection" : qUnion([Q1]), "distance" : 25 * mm, "makeCopy" : false});
        }
        {
            var Q0;
            Q0=makeQuery(id+"FCm0gpzPxwSbBdX_7.opPattern","COPY",BODY,{"derivedFrom":makeQuery(id+"F20.opExtrude","SWEPT_BODY",BODY,{"disambiguationData":[OSD([sQuery(id+"F1.wireOp",EDGE,"E0.top"),sQuery(id+"F19.wireOp",EDGE,"E57"),sQuery(id+"F19.wireOp",EDGE,"E58"),sQuery(id+"F19.wireOp",EDGE,"E59"),sQuery(id+"F19.wireOp",EDGE,"E60"),sQuery(id+"F19.wireOp",EDGE,"E61"),sQuery(id+"F19.wireOp",EDGE,"E62.trimOffspring"),sQuery(id+"F19.wireOp",EDGE,"treZg7xo-gXZQ-1tuO-3OQy-4RqyVRKiaork"),sQuery(id+"F19.wireOp",EDGE,"E63"),sQuery(id+"F19.wireOp",EDGE,"49c95767-d3e9-4f83-846b-7651090b67ab.trimOffspring")])]}),"instanceName":"1"});
            var Q1;
            Q1=makeQuery(id+"F26.opPattern","COPY",BODY,{"derivedFrom":makeQuery(id+"F25.opPattern","COPY",BODY,{"derivedFrom":makeQuery(id+"F24.opPattern","COPY",BODY,{"derivedFrom":makeQuery(id+"F23.opExtrude","SWEPT_BODY",BODY,{"disambiguationData":[OSD([sQuery(id+"F22.wireOp",EDGE,"E72"),sQuery(id+"F22.wireOp",EDGE,"E73.bottom"),sQuery(id+"F22.wireOp",EDGE,"E73.top"),sQuery(id+"F22.wireOp",EDGE,"E73.left"),sQuery(id+"F22.wireOp",EDGE,"E73.right")])]}),"instanceName":"1"}),"instanceName":"1"}),"instanceName":"1"});
            var Q2;
            Q2=makeQuery(id+"F24.opPattern","COPY",BODY,{"derivedFrom":makeQuery(id+"F23.opExtrude","SWEPT_BODY",BODY,{"disambiguationData":[OSD([sQuery(id+"F22.wireOp",EDGE,"E72"),sQuery(id+"F22.wireOp",EDGE,"E73.bottom"),sQuery(id+"F22.wireOp",EDGE,"E73.top"),sQuery(id+"F22.wireOp",EDGE,"E73.left"),sQuery(id+"F22.wireOp",EDGE,"E73.right")])]}),"instanceName":"1"});
            var Q3;
            Q3=makeQuery(id+"F25.opPattern","COPY",BODY,{"derivedFrom":makeQuery(id+"F24.opPattern","COPY",BODY,{"derivedFrom":makeQuery(id+"F23.opExtrude","SWEPT_BODY",BODY,{"disambiguationData":[OSD([sQuery(id+"F22.wireOp",EDGE,"E72"),sQuery(id+"F22.wireOp",EDGE,"E73.bottom"),sQuery(id+"F22.wireOp",EDGE,"E73.top"),sQuery(id+"F22.wireOp",EDGE,"E73.left"),sQuery(id+"F22.wireOp",EDGE,"E73.right")])]}),"instanceName":"1"}),"instanceName":"1"});
            var Q4;
            Q4=qCreatedBy(makeId("Top.planeOp"),FACE);
            transform(context, id + "F36", {"entities" : qUnion([Q0, Q1, Q2, Q3]), "transformType" : TransformType.TRANSLATION_DISTANCE, "transformDirection" : qUnion([Q4]), "distance" : 25 * mm, "makeCopy" : false});
        }
        {
            var Q0;
            Q0=makeQuery(id+"F6.opExtrude","SWEPT_BODY",BODY,{"disambiguationData":[OSD([sQuery(id+"F4.wireOp",EDGE,"E24.left"),sQuery(id+"F4.wireOp",EDGE,"E25.MirrorCS"),sQuery(id+"F4.wireOp",EDGE,"E26.MirrorCS"),sQuery(id+"F4.wireOp",EDGE,"E27.MirrorCS"),sQuery(id+"F4.wireOp",EDGE,"E33.bottom"),sQuery(id+"F4.wireOp",EDGE,"E33.top"),sQuery(id+"F4.wireOp",EDGE,"E33.right"),sQuery(id+"F4.wireOp",EDGE,"E34.bottom"),sQuery(id+"F4.wireOp",EDGE,"E34.top"),sQuery(id+"F4.wireOp",EDGE,"E34.left"),sQuery(id+"F4.wireOp",EDGE,"E35.trimOffspring"),sQuery(id+"F4.wireOp",EDGE,"E36.trimOffspring")])]});
            transform(context, id + "F37", {"entities" : qUnion([Q0]), "transformType" : TransformType.TRANSLATION_3D, "dx" : 0 * mm, "dy" : 0 * mm, "dz" : 73 * mm, "makeCopy" : true});
        }
        {
            var Q0;
            Q0=makeQuery(id+"F37.opPattern","COPY",BODY,{"derivedFrom":makeQuery(id+"F6.opExtrude","SWEPT_BODY",BODY,{"disambiguationData":[OSD([sQuery(id+"F4.wireOp",EDGE,"E24.left"),sQuery(id+"F4.wireOp",EDGE,"E25.MirrorCS"),sQuery(id+"F4.wireOp",EDGE,"E26.MirrorCS"),sQuery(id+"F4.wireOp",EDGE,"E27.MirrorCS"),sQuery(id+"F4.wireOp",EDGE,"E33.bottom"),sQuery(id+"F4.wireOp",EDGE,"E33.top"),sQuery(id+"F4.wireOp",EDGE,"E33.right"),sQuery(id+"F4.wireOp",EDGE,"E34.bottom"),sQuery(id+"F4.wireOp",EDGE,"E34.top"),sQuery(id+"F4.wireOp",EDGE,"E34.left"),sQuery(id+"F4.wireOp",EDGE,"E35.trimOffspring"),sQuery(id+"F4.wireOp",EDGE,"E36.trimOffspring")])]}),"instanceName":"1"});
            var Q1;
            Q1=makeQuery(id+"F7.opPattern","COPY",BODY,{"derivedFrom":makeQuery(id+"F2.opExtrude","SWEPT_BODY",BODY,{"disambiguationData":[OSD([sQuery(id+"F1.wireOp",EDGE,"E0.bottom"),sQuery(id+"F1.wireOp",EDGE,"E0.top"),sQuery(id+"F1.wireOp",EDGE,"E0.left"),sQuery(id+"F1.wireOp",EDGE,"E2.bottom"),sQuery(id+"F1.wireOp",EDGE,"E2.top"),sQuery(id+"F1.wireOp",EDGE,"E2.left"),sQuery(id+"F1.wireOp",EDGE,"E3.bottom"),sQuery(id+"F1.wireOp",EDGE,"E3.top"),sQuery(id+"F1.wireOp",EDGE,"E3.right"),sQuery(id+"F1.wireOp",EDGE,"E5.trimOffspring"),sQuery(id+"F1.wireOp",EDGE,"E7.bottom"),sQuery(id+"F1.wireOp",EDGE,"E7.left"),sQuery(id+"F1.wireOp",EDGE,"E7.right"),sQuery(id+"F1.wireOp",EDGE,"E8.trimOffspring"),sQuery(id+"F1.wireOp",EDGE,"E9.bottom"),sQuery(id+"F1.wireOp",EDGE,"E9.left"),sQuery(id+"F1.wireOp",EDGE,"E9.right"),sQuery(id+"F1.wireOp",EDGE,"E10.trimOffspring"),sQuery(id+"F1.wireOp",EDGE,"E11.MirrorCS"),sQuery(id+"F1.wireOp",EDGE,"E12.MirrorCS"),sQuery(id+"F1.wireOp",EDGE,"E13.MirrorCS"),sQuery(id+"F1.wireOp",EDGE,"E14.MirrorCS"),sQuery(id+"F1.wireOp",EDGE,"E15.MirrorCS"),sQuery(id+"F1.wireOp",EDGE,"E18.MirrorCS"),sQuery(id+"F1.wireOp",EDGE,"E19.MirrorCS"),sQuery(id+"F1.wireOp",EDGE,"E20.MirrorCS"),sQuery(id+"F1.wireOp",EDGE,"E21"),sQuery(id+"F1.wireOp",EDGE,"E22")])]}),"instanceName":"1"});
            var Q2;
            Q2=makeQuery(id+"F5.opExtrude","SWEPT_BODY",BODY,{"disambiguationData":[OSD([sQuery(id+"F3.wireOp",EDGE,"E23.bottom"),sQuery(id+"F3.wireOp",EDGE,"E23.top"),sQuery(id+"F3.wireOp",EDGE,"E23.left"),sQuery(id+"F3.wireOp",EDGE,"E23.right")])]});
            var Q3;
            Q3=makeQuery(id+"F9.opPattern","COPY",BODY,{"derivedFrom":makeQuery(id+"F5.opExtrude","SWEPT_BODY",BODY,{"disambiguationData":[OSD([sQuery(id+"F3.wireOp",EDGE,"E23.bottom"),sQuery(id+"F3.wireOp",EDGE,"E23.top"),sQuery(id+"F3.wireOp",EDGE,"E23.left"),sQuery(id+"F3.wireOp",EDGE,"E23.right")])]}),"instanceName":"1"});
            var Q4;
            Q4=makeQuery(id+"F2.opExtrude","SWEPT_BODY",BODY,{"disambiguationData":[OSD([sQuery(id+"F1.wireOp",EDGE,"E0.bottom"),sQuery(id+"F1.wireOp",EDGE,"E0.top"),sQuery(id+"F1.wireOp",EDGE,"E0.left"),sQuery(id+"F1.wireOp",EDGE,"E2.bottom"),sQuery(id+"F1.wireOp",EDGE,"E2.top"),sQuery(id+"F1.wireOp",EDGE,"E2.left"),sQuery(id+"F1.wireOp",EDGE,"E3.bottom"),sQuery(id+"F1.wireOp",EDGE,"E3.top"),sQuery(id+"F1.wireOp",EDGE,"E3.right"),sQuery(id+"F1.wireOp",EDGE,"E5.trimOffspring"),sQuery(id+"F1.wireOp",EDGE,"E7.bottom"),sQuery(id+"F1.wireOp",EDGE,"E7.left"),sQuery(id+"F1.wireOp",EDGE,"E7.right"),sQuery(id+"F1.wireOp",EDGE,"E8.trimOffspring"),sQuery(id+"F1.wireOp",EDGE,"E9.bottom"),sQuery(id+"F1.wireOp",EDGE,"E9.left"),sQuery(id+"F1.wireOp",EDGE,"E9.right"),sQuery(id+"F1.wireOp",EDGE,"E10.trimOffspring"),sQuery(id+"F1.wireOp",EDGE,"E11.MirrorCS"),sQuery(id+"F1.wireOp",EDGE,"E12.MirrorCS"),sQuery(id+"F1.wireOp",EDGE,"E13.MirrorCS"),sQuery(id+"F1.wireOp",EDGE,"E14.MirrorCS"),sQuery(id+"F1.wireOp",EDGE,"E15.MirrorCS"),sQuery(id+"F1.wireOp",EDGE,"E18.MirrorCS"),sQuery(id+"F1.wireOp",EDGE,"E19.MirrorCS"),sQuery(id+"F1.wireOp",EDGE,"E20.MirrorCS"),sQuery(id+"F1.wireOp",EDGE,"E21"),sQuery(id+"F1.wireOp",EDGE,"E22")])]});
            booleanBodies(context, id + "F38", {"operationType" : BooleanOperationType.SUBTRACTION, "tools" : qUnion([Q0]), "targets" : qUnion([Q1, Q2, Q3, Q4]), "keepTools" : true});
        }
        {
            var Q0;
            Q0=makeQuery(id+"F11.opPattern","COPY",BODY,{"derivedFrom":makeQuery(id+"F6.opExtrude","SWEPT_BODY",BODY,{"disambiguationData":[OSD([sQuery(id+"F4.wireOp",EDGE,"E24.left"),sQuery(id+"F4.wireOp",EDGE,"E25.MirrorCS"),sQuery(id+"F4.wireOp",EDGE,"E26.MirrorCS"),sQuery(id+"F4.wireOp",EDGE,"E27.MirrorCS"),sQuery(id+"F4.wireOp",EDGE,"E33.bottom"),sQuery(id+"F4.wireOp",EDGE,"E33.top"),sQuery(id+"F4.wireOp",EDGE,"E33.right"),sQuery(id+"F4.wireOp",EDGE,"E34.bottom"),sQuery(id+"F4.wireOp",EDGE,"E34.top"),sQuery(id+"F4.wireOp",EDGE,"E34.left"),sQuery(id+"F4.wireOp",EDGE,"E35.trimOffspring"),sQuery(id+"F4.wireOp",EDGE,"E36.trimOffspring")])]}),"instanceName":"1"});
            var Q1;
            Q1=makeQuery(id+"F5.opExtrude","SWEPT_BODY",BODY,{"disambiguationData":[OSD([sQuery(id+"F3.wireOp",EDGE,"E23.bottom"),sQuery(id+"F3.wireOp",EDGE,"E23.top"),sQuery(id+"F3.wireOp",EDGE,"E23.left"),sQuery(id+"F3.wireOp",EDGE,"E23.right")])]});
            var Q2;
            Q2=makeQuery(id+"F7.opPattern","COPY",BODY,{"derivedFrom":makeQuery(id+"F2.opExtrude","SWEPT_BODY",BODY,{"disambiguationData":[OSD([sQuery(id+"F1.wireOp",EDGE,"E0.bottom"),sQuery(id+"F1.wireOp",EDGE,"E0.top"),sQuery(id+"F1.wireOp",EDGE,"E0.left"),sQuery(id+"F1.wireOp",EDGE,"E2.bottom"),sQuery(id+"F1.wireOp",EDGE,"E2.top"),sQuery(id+"F1.wireOp",EDGE,"E2.left"),sQuery(id+"F1.wireOp",EDGE,"E3.bottom"),sQuery(id+"F1.wireOp",EDGE,"E3.top"),sQuery(id+"F1.wireOp",EDGE,"E3.right"),sQuery(id+"F1.wireOp",EDGE,"E5.trimOffspring"),sQuery(id+"F1.wireOp",EDGE,"E7.bottom"),sQuery(id+"F1.wireOp",EDGE,"E7.left"),sQuery(id+"F1.wireOp",EDGE,"E7.right"),sQuery(id+"F1.wireOp",EDGE,"E8.trimOffspring"),sQuery(id+"F1.wireOp",EDGE,"E9.bottom"),sQuery(id+"F1.wireOp",EDGE,"E9.left"),sQuery(id+"F1.wireOp",EDGE,"E9.right"),sQuery(id+"F1.wireOp",EDGE,"E10.trimOffspring"),sQuery(id+"F1.wireOp",EDGE,"E11.MirrorCS"),sQuery(id+"F1.wireOp",EDGE,"E12.MirrorCS"),sQuery(id+"F1.wireOp",EDGE,"E13.MirrorCS"),sQuery(id+"F1.wireOp",EDGE,"E14.MirrorCS"),sQuery(id+"F1.wireOp",EDGE,"E15.MirrorCS"),sQuery(id+"F1.wireOp",EDGE,"E18.MirrorCS"),sQuery(id+"F1.wireOp",EDGE,"E19.MirrorCS"),sQuery(id+"F1.wireOp",EDGE,"E20.MirrorCS"),sQuery(id+"F1.wireOp",EDGE,"E21"),sQuery(id+"F1.wireOp",EDGE,"E22")])]}),"instanceName":"1"});
            var Q3;
            Q3=makeQuery(id+"F9.opPattern","COPY",BODY,{"derivedFrom":makeQuery(id+"F5.opExtrude","SWEPT_BODY",BODY,{"disambiguationData":[OSD([sQuery(id+"F3.wireOp",EDGE,"E23.bottom"),sQuery(id+"F3.wireOp",EDGE,"E23.top"),sQuery(id+"F3.wireOp",EDGE,"E23.left"),sQuery(id+"F3.wireOp",EDGE,"E23.right")])]}),"instanceName":"1"});
            var Q4;
            Q4=makeQuery(id+"F2.opExtrude","SWEPT_BODY",BODY,{"disambiguationData":[OSD([sQuery(id+"F1.wireOp",EDGE,"E0.bottom"),sQuery(id+"F1.wireOp",EDGE,"E0.top"),sQuery(id+"F1.wireOp",EDGE,"E0.left"),sQuery(id+"F1.wireOp",EDGE,"E2.bottom"),sQuery(id+"F1.wireOp",EDGE,"E2.top"),sQuery(id+"F1.wireOp",EDGE,"E2.left"),sQuery(id+"F1.wireOp",EDGE,"E3.bottom"),sQuery(id+"F1.wireOp",EDGE,"E3.top"),sQuery(id+"F1.wireOp",EDGE,"E3.right"),sQuery(id+"F1.wireOp",EDGE,"E5.trimOffspring"),sQuery(id+"F1.wireOp",EDGE,"E7.bottom"),sQuery(id+"F1.wireOp",EDGE,"E7.left"),sQuery(id+"F1.wireOp",EDGE,"E7.right"),sQuery(id+"F1.wireOp",EDGE,"E8.trimOffspring"),sQuery(id+"F1.wireOp",EDGE,"E9.bottom"),sQuery(id+"F1.wireOp",EDGE,"E9.left"),sQuery(id+"F1.wireOp",EDGE,"E9.right"),sQuery(id+"F1.wireOp",EDGE,"E10.trimOffspring"),sQuery(id+"F1.wireOp",EDGE,"E11.MirrorCS"),sQuery(id+"F1.wireOp",EDGE,"E12.MirrorCS"),sQuery(id+"F1.wireOp",EDGE,"E13.MirrorCS"),sQuery(id+"F1.wireOp",EDGE,"E14.MirrorCS"),sQuery(id+"F1.wireOp",EDGE,"E15.MirrorCS"),sQuery(id+"F1.wireOp",EDGE,"E18.MirrorCS"),sQuery(id+"F1.wireOp",EDGE,"E19.MirrorCS"),sQuery(id+"F1.wireOp",EDGE,"E20.MirrorCS"),sQuery(id+"F1.wireOp",EDGE,"E21"),sQuery(id+"F1.wireOp",EDGE,"E22")])]});
            booleanBodies(context, id + "F39", {"operationType" : BooleanOperationType.SUBTRACTION, "tools" : qUnion([Q0]), "targets" : qUnion([Q1, Q2, Q3, Q4]), "keepTools" : true});
        }
        {
            var Q0;
            Q0=makeQuery(id+"F37.opPattern","COPY",FACE,{"derivedFrom":makeQuery(id+"F6.opExtrude","CAP_FACE",FACE,{"disambiguationData":[OSD([sQuery(id+"F4.wireOp",EDGE,"E24.left"),sQuery(id+"F4.wireOp",EDGE,"E25.MirrorCS"),sQuery(id+"F4.wireOp",EDGE,"E26.MirrorCS"),sQuery(id+"F4.wireOp",EDGE,"E27.MirrorCS"),sQuery(id+"F4.wireOp",EDGE,"E33.bottom"),sQuery(id+"F4.wireOp",EDGE,"E33.top"),sQuery(id+"F4.wireOp",EDGE,"E33.right"),sQuery(id+"F4.wireOp",EDGE,"E34.bottom"),sQuery(id+"F4.wireOp",EDGE,"E34.top"),sQuery(id+"F4.wireOp",EDGE,"E34.left"),sQuery(id+"F4.wireOp",EDGE,"E35.trimOffspring"),sQuery(id+"F4.wireOp",EDGE,"E36.trimOffspring")])],"isStart":false}),"instanceName":"1"});
            var sketch = newSketch(context, id + "F40", { "sketchPlane" : qUnion([Q0])});
            skPoint(sketch, "E77.oppositeSnap0", {"position": v(-22.5, -3) * mm});
            skLineSegment(sketch, "E77.bottom", {"start": v(-10, -3) * mm, "end": v(-22.5, -3) * mm});
            skLineSegment(sketch, "E77.top", {"start": v(-13, -23.5) * mm, "end": v(-19.5, -23.5) * mm});
            skLineSegment(sketch, "E77.left", {"start": v(-10, -3) * mm, "end": v(-10, -20.5) * mm});
            skLineSegment(sketch, "E77.right", {"start": v(-22.5, -3) * mm, "end": v(-22.5, -20.5) * mm});
            skPoint(sketch, "E78.oppositeSnap0", {"position": v(22.5, -3) * mm});
            skLineSegment(sketch, "E78.bottom", {"start": v(10, -3) * mm, "end": v(22.5, -3) * mm});
            skLineSegment(sketch, "E78.top", {"start": v(13, -23.5) * mm, "end": v(19.5, -23.5) * mm});
            skLineSegment(sketch, "E78.left", {"start": v(10, -3) * mm, "end": v(10, -20.5) * mm});
            skLineSegment(sketch, "E78.right", {"start": v(22.5, -3) * mm, "end": v(22.5, -20.5) * mm});
            skPoint(sketch, "E79.visualSharp", {"position": v(-10, -23.5) * mm});
            skArc(sketch, "E79.filletArc", {"start": v(-13, -23.5) * mm, "mid": v(-10.88, -22.63) * mm, "end": v(-10, -20.5) * mm});
            skPoint(sketch, "E80.visualSharp", {"position": v(-22.5, -23.5) * mm});
            skArc(sketch, "E80.filletArc", {"start": v(-22.5, -20.5) * mm, "mid": v(-21.62, -22.63) * mm, "end": v(-19.5, -23.5) * mm});
            skPoint(sketch, "E81.visualSharp", {"position": v(10, -23.5) * mm});
            skArc(sketch, "E81.filletArc", {"start": v(10, -20.5) * mm, "mid": v(10.88, -22.63) * mm, "end": v(13, -23.5) * mm});
            skPoint(sketch, "E82.visualSharp", {"position": v(22.5, -23.5) * mm});
            skArc(sketch, "E82.filletArc", {"start": v(19.5, -23.5) * mm, "mid": v(21.62, -22.63) * mm, "end": v(22.5, -20.5) * mm});
            skSolve(sketch);
        }
        {
            var Q0;
            Q0=makeQuery(id+"F40.imprint","IMPRINT",FACE,{"disambiguationData":[TD([[makeQuery(id+"F40.imprint","IMPRINT",EDGE,{"derivedFrom":sQuery(id+"F40.wireOp",EDGE,"E77.bottom")}),1.0]])]});
            var Q1;
            Q1=makeQuery(id+"F40.imprint","IMPRINT",FACE,{"disambiguationData":[TD([[makeQuery(id+"F40.imprint","IMPRINT",EDGE,{"derivedFrom":sQuery(id+"F40.wireOp",EDGE,"E78.bottom")}),1.0]])]});
            extrude(context, id + "F41", {"entities" : qUnion([Q0, Q1]), "operationType" : NewBodyOperationType.REMOVE, "oppositeDirection" : true, "depth" : (getVariable(context, 'w')) * mm, "offsetDistance" : 25 * mm});
        }
        {
            var Q0;
            {var subQ8=sQuery(id+"F19.wireOp",EDGE,"E57");Q0=makeQuery(id+"F19.imprint","IMPRINT",FACE,{"disambiguationData":[TD([[makeQuery(id+"F19.imprint","IMPRINT",EDGE,{"derivedFrom":subQ8}),-1.0]])]});}
            var Q1;
            Q1=makeQuery(id+"F19.imprint","IMPRINT",FACE,{"disambiguationData":[TD([[makeQuery(id+"F19.imprint","IMPRINT",EDGE,{"derivedFrom":sQuery(id+"F19.wireOp",EDGE,"E64")}),-1.0]])]});
            var Q2;
            {var subQ4=sQuery(id+"F19.wireOp",EDGE,"E63");Q2=makeQuery(id+"F19.imprint","IMPRINT",FACE,{"disambiguationData":[TD([[makeQuery(id+"F19.imprint","IMPRINT",EDGE,{"derivedFrom":subQ4}),-1.0]])]});}
            extrude(context, id + "F42", {"entities" : qUnion([Q0, Q1, Q2]), "depth" : (getVariable(context, 'w')) * mm, "offsetDistance" : 25 * mm});
        }
        {
            var Q0;
            Q0=makeQuery(id+"F42.opExtrude","SWEPT_BODY",BODY,{"disambiguationData":[OSD([sQuery(id+"F19.wireOp",EDGE,"E57"),sQuery(id+"F19.wireOp",EDGE,"E58"),sQuery(id+"F19.wireOp",EDGE,"E59"),sQuery(id+"F19.wireOp",EDGE,"E60"),sQuery(id+"F19.wireOp",EDGE,"E61"),sQuery(id+"F19.wireOp",EDGE,"E62.trimOffspring"),sQuery(id+"F19.wireOp",EDGE,"treZg7xo-gXZQ-1tuO-3OQy-4RqyVRKiaork"),sQuery(id+"F19.wireOp",EDGE,"E63"),sQuery(id+"F19.wireOp",EDGE,"49c95767-d3e9-4f83-846b-7651090b67ab.trimOffspring"),sQuery(id+"F19.wireOp",EDGE,"E64"),sQuery(id+"F19.wireOp",EDGE,"E65.filletArc"),sQuery(id+"F19.wireOp",EDGE,"E66.filletArc")])]});
            transform(context, id + "F43", {"entities" : qUnion([Q0]), "transformType" : TransformType.TRANSLATION_3D, "dx" : 0 * mm, "dy" : 30.6 * mm, "dz" : 0 * mm, "makeCopy" : true});
        }
        {
            var Q0;
            Q0=makeQuery(id+"F42.opExtrude","SWEPT_BODY",BODY,{"disambiguationData":[OSD([sQuery(id+"F19.wireOp",EDGE,"E57"),sQuery(id+"F19.wireOp",EDGE,"E58"),sQuery(id+"F19.wireOp",EDGE,"E59"),sQuery(id+"F19.wireOp",EDGE,"E60"),sQuery(id+"F19.wireOp",EDGE,"E61"),sQuery(id+"F19.wireOp",EDGE,"E62.trimOffspring"),sQuery(id+"F19.wireOp",EDGE,"treZg7xo-gXZQ-1tuO-3OQy-4RqyVRKiaork"),sQuery(id+"F19.wireOp",EDGE,"E63"),sQuery(id+"F19.wireOp",EDGE,"49c95767-d3e9-4f83-846b-7651090b67ab.trimOffspring"),sQuery(id+"F19.wireOp",EDGE,"E64"),sQuery(id+"F19.wireOp",EDGE,"E65.filletArc"),sQuery(id+"F19.wireOp",EDGE,"E66.filletArc")])]});
            var Q1;
            {var subQ1=sQuery(id+"F19.wireOp",EDGE,"E57");Q1=makeQuery(id+"F19.imprint","IMPRINT",FACE,{"disambiguationData":[TD([[makeQuery(id+"F19.imprint","IMPRINT",EDGE,{"derivedFrom":subQ1}),-1.0]])]});}
            transform(context, id + "F44", {"entities" : qUnion([Q0]), "transformType" : TransformType.TRANSLATION_DISTANCE, "transformDirection" : qUnion([Q1]), "distance" : 27.5 * mm, "oppositeDirection" : true, "makeCopy" : false});
        }
    });
